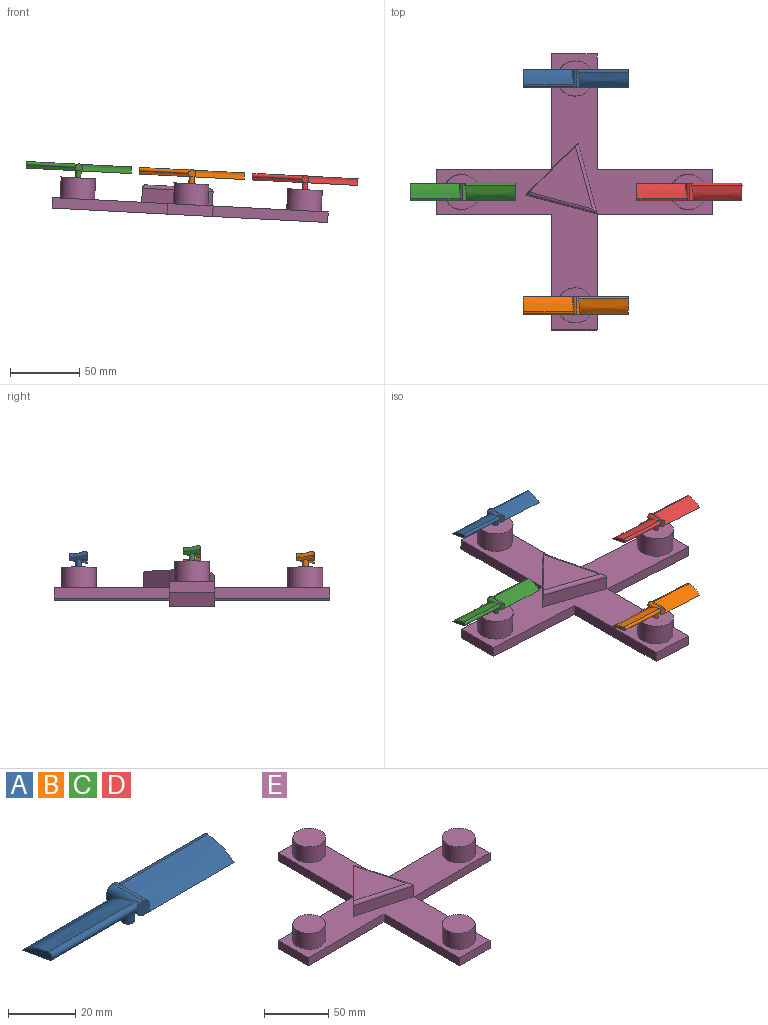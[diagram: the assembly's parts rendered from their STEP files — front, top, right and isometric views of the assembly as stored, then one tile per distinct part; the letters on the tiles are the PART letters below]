
ASSEMBLY  parts=5 mates=4
PART A: 17 faces, bbox 76.4x14.1x10.3 mm
  f0: plane 3.4x2.57mm, normal (1,0,0), area 4mm2, adj f1,f5,f14
  f1: plane 5.23x5.23mm, normal (0,-1,0), area 22mm2, adj f0,f6,f14,f15
  f2: plane 5.23x5.23mm, normal (0,1,0), area 22mm2, adj f3,f9,f14,f15,f16
  f3: plane 3.4x2.57mm, normal (-1,0,0), area 4mm2, adj f2,f8,f15
  f4: cylinder r=1.39mm len=36.65mm, axis (1,0,0), area 157.1mm2, adj f5,f6,f7,f14,f16
  f5: extruded ~36.65x10.98mm, area 438.1mm2, adj f0,f4,f6,f7,f14
  f6: plane 38.1x11.47mm, normal (0,0.18,-0.98), area 422mm2, adj f1,f4,f5,f7,f16
  f7: plane 12.61x4.8mm, normal (1,0,0), area 27.2mm2, adj f4,f5,f6
  f8: extruded ~36.9x10.98mm, area 439.1mm2, adj f3,f9,f10,f11,f15
  f9: plane 38.1x11.47mm, normal (0,-0.18,-0.98), area 422mm2, adj f2,f8,f10,f11,f15
  f10: cylinder r=1.39mm len=36.9mm, axis (1,0,0), area 157.6mm2, adj f8,f9,f11,f15
  f11: plane 12.61x4.8mm, normal (-1,0,0), area 27.2mm2, adj f8,f9,f10
  f12: cylinder r=1.91mm len=5.08mm, axis (0,0,1), area 60.8mm2, adj f13,f15,f16
  f13: plane 3.81x3.81mm, normal (0,0,-1), area 11.4mm2, adj f12
  f14: bspline ~13.97x2.54mm, area 37.8mm2, adj f0,f1,f2,f4,f5,f15,f16
  f15: cylinder r=2.54mm len=12.7mm, axis (0,1,0), area 60.7mm2, adj f1,f2,f3,f8,f9,f10,f12,f14
  f16: cylinder r=2.54mm len=12.7mm, axis (0,1,0), area 24.3mm2, adj f2,f4,f6,f12,f14,f15
PART B: same geometry as A
PART C: same geometry as A
PART D: same geometry as A
PART E: 29 faces, bbox 199.9x199.9x22.9 mm
  f0: plane 83.44x7.62mm, normal (1,0,0), area 635.8mm2, adj f1,f11,f12,f13
  f1: plane 33.02x7.62mm, normal (0,1,0), area 251.6mm2, adj f0,f2,f12,f13
  f2: plane 83.44x20.32mm, normal (-1,0,0), area 637.3mm2, adj f1,f3,f12,f13,f25,f26
  f3: plane 83.44x20.32mm, normal (0,1,0), area 637.3mm2, adj f2,f4,f12,f13,f22,f26
  f4: plane 33.02x7.62mm, normal (-1,0,0), area 251.6mm2, adj f3,f5,f12,f13
  f5: plane 83.44x7.62mm, normal (0,-1,0), area 635.8mm2, adj f4,f6,f12,f13
  f6: plane 83.44x7.62mm, normal (-1,0,0), area 635.8mm2, adj f5,f7,f12,f13
  f7: plane 33.02x7.62mm, normal (0,-1,0), area 251.6mm2, adj f6,f8,f12,f13
  f8: plane 83.44x7.62mm, normal (1,0,0), area 635.8mm2, adj f7,f9,f12,f13
  f9: plane 83.44x7.62mm, normal (0,-1,0), area 635.8mm2, adj f8,f10,f12,f13
  f10: plane 33.02x7.62mm, normal (1,0,0), area 251.6mm2, adj f9,f11,f12,f13
  f11: plane 83.44x7.62mm, normal (0,1,0), area 635.8mm2, adj f0,f10,f12,f13
  f12: plane 199.9x199.9mm, normal (0,0,1), area 8863.9mm2, adj f0,f1,f2,f3,f4,f5,f6,f7
  f13: plane 199.9x199.9mm, normal (0,0,-1), area 12110.9mm2, adj f0,f1,f2,f3,f4,f5,f6,f7
  f14: cylinder r=12.7mm len=25.4mm, axis (0,0,-1), area 1216.1mm2, adj f12,f15
  f15: plane 25.4x25.4mm, normal (0,0,1), area 506.7mm2, adj f14
  f16: cylinder r=12.7mm len=25.4mm, axis (0,0,-1), area 1216.1mm2, adj f12,f17
  f17: plane 25.4x25.4mm, normal (0,0,1), area 506.7mm2, adj f16
  f18: cylinder r=12.7mm len=25.4mm, axis (0,0,-1), area 1216.1mm2, adj f12,f19
  f19: plane 25.4x25.4mm, normal (0,0,1), area 506.7mm2, adj f18
  f20: cylinder r=12.7mm len=25.4mm, axis (0,0,-1), area 1216.1mm2, adj f12,f21
  f21: plane 25.4x25.4mm, normal (0,0,1), area 506.7mm2, adj f20
  f22: plane 18.71x18.71mm, normal (-0.71,0.71,0), area 334.4mm2, adj f3,f12,f23,f26,f27
  f23: plane 51.28x13.74mm, normal (-0.26,-0.97,0), area 539.3mm2, adj f12,f22,f24,f27
  f24: plane 51.28x13.74mm, normal (0.97,0.26,0), area 539.3mm2, adj f12,f23,f25,f28
  f25: plane 18.71x18.71mm, normal (-0.71,0.71,0), area 334.4mm2, adj f2,f12,f24,f26,f28
  f26: plane 45.61x45.61mm, normal (0,0,1), area 965.4mm2, adj f2,f3,f22,f25,f27,f28
  f27: cylinder r=2.54mm len=51.93mm, axis (-0.97,0.26,0), area 203.3mm2, adj f22,f23,f26,f28
  f28: cylinder r=2.54mm len=51.93mm, axis (0.26,-0.97,0), area 203.3mm2, adj f24,f25,f26,f27
PLACE A rot(axis=(0,1,0),3deg) t=(-143.96,-22.58,7.79)mm
PLACE B rot(axis=(0,1,0),3deg) t=(-143.96,-186.92,7.79)mm
PLACE C rot(axis=(0,1,0),3deg) t=(-226.01,-104.75,12.08)mm
PLACE D rot(axis=(0,1,0),3deg) t=(-61.9,-104.75,3.5)mm
PLACE E rot(axis=(0,1,0),3deg) t=(-19.73,-90.14,-26.68)mm
MATE fastened D.f12 <-> E.f18  axis (-0.05,0,-1) through (-62.17,-104.75,-1.57)mm
MATE fastened C.f12 <-> E.f14  axis (-0.05,0,-1) through (-226.28,-104.75,7.01)mm
MATE fastened B.f12 <-> E.f20  axis (0.05,0,1) through (-144.22,-186.92,2.72)mm
MATE fastened A.f12 <-> E.f16  axis (-0.05,0,-1) through (-144.22,-22.58,2.72)mm
